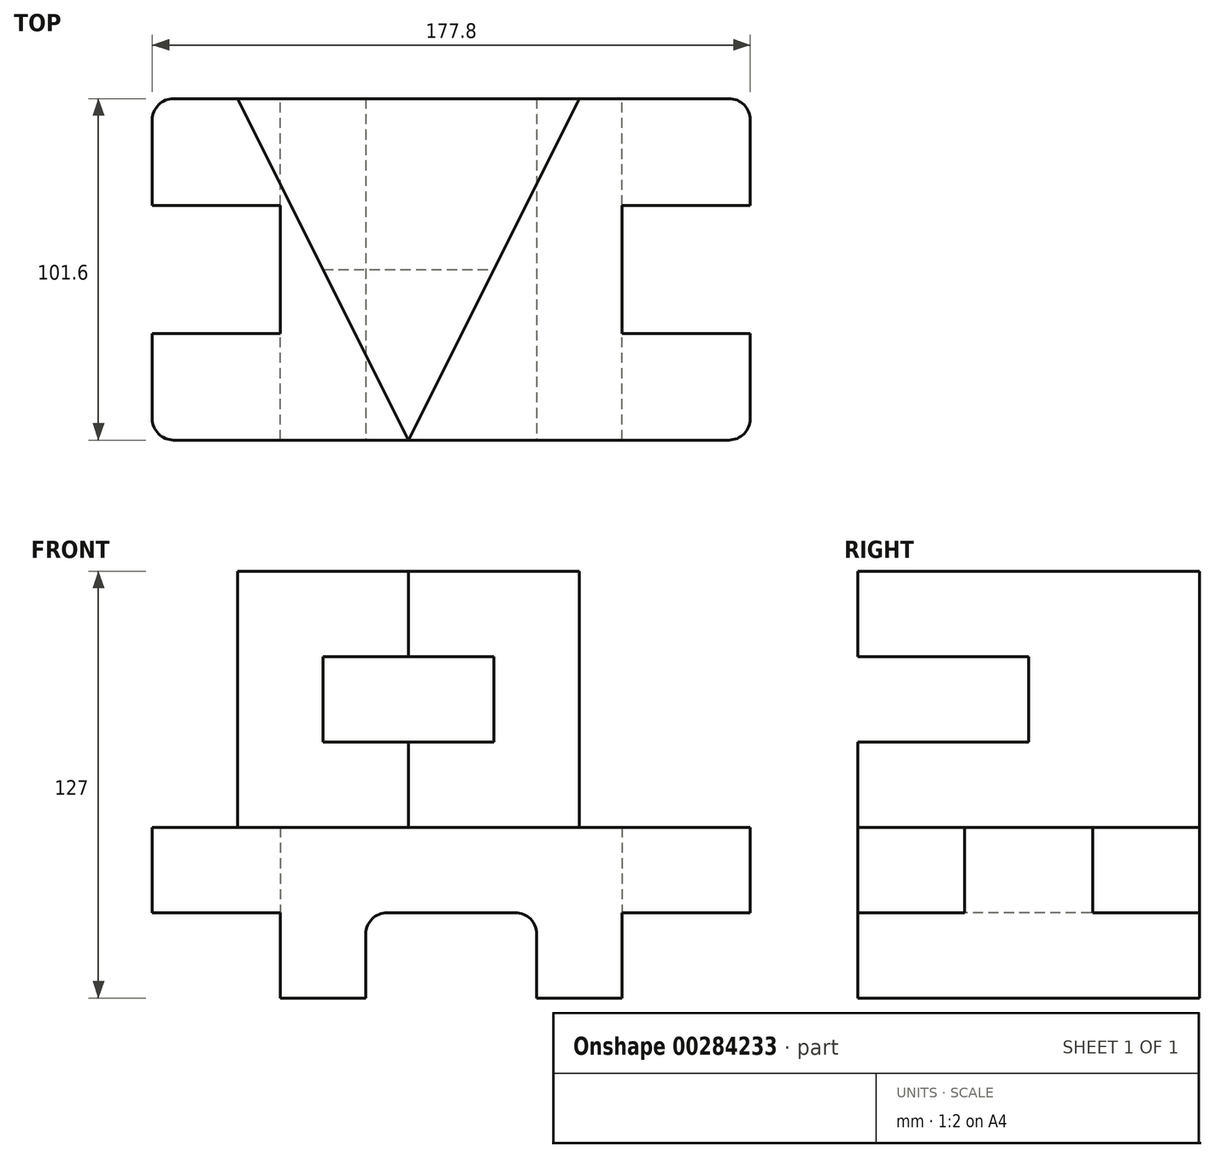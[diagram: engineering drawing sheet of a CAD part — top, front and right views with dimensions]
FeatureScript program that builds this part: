
annotation { "Feature Type Name" : "Feature", "Feature Type Description" : "" }
export const myFeature = defineFeature(function(context is Context, id is Id, definition is map)
    precondition{}
    {
        {
            var Q0;
            Q0=qCreatedBy(makeId("Front.planeOp"),FACE);
            var sketch = newSketch(context, id + "F0", { "sketchPlane" : qUnion([Q0])});
            skLineSegment(sketch, "E0", {"start": v(0, 0) * mm, "end": v(0, 25.4) * mm});
            skLineSegment(sketch, "E1", {"start": v(0, 25.4) * mm, "end": v(-38.1, 25.4) * mm});
            skLineSegment(sketch, "E2", {"start": v(-38.1, 25.4) * mm, "end": v(-38.1, 50.8) * mm});
            skLineSegment(sketch, "E3", {"start": v(-38.1, 50.8) * mm, "end": v(139.7, 50.8) * mm});
            skLineSegment(sketch, "E4", {"start": v(139.7, 50.8) * mm, "end": v(139.7, 25.4) * mm});
            skLineSegment(sketch, "E5", {"start": v(139.7, 25.4) * mm, "end": v(101.6, 25.4) * mm});
            skLineSegment(sketch, "E6", {"start": v(101.6, 25.4) * mm, "end": v(101.6, 0) * mm});
            skLineSegment(sketch, "E7", {"start": v(101.6, 0) * mm, "end": v(0, 0) * mm});
            skSolve(sketch);
        }
        {
            var Q0;
            Q0 = qSketchRegion(id + "F0", true);
            extrude(context, id + "F1", {"entities" : qUnion([Q0]), "depth" : 101.6 * mm});
        }
        {
            var Q0;
            Q0=makeQuery(id+"F1.opExtrude","SWEPT_FACE",FACE,{"disambiguationData":[OSD([sQuery(id+"F0.wireOp",EDGE,"E4")])]});
            var sketch = newSketch(context, id + "F2", { "sketchPlane" : qUnion([Q0])});
            skLineSegment(sketch, "E8.bottom", {"start": v(-69.85, 50.8) * mm, "end": v(-31.75, 50.8) * mm});
            skLineSegment(sketch, "E8.top", {"start": v(-69.85, 25.4) * mm, "end": v(-31.75, 25.4) * mm});
            skLineSegment(sketch, "E8.left", {"start": v(-69.85, 50.8) * mm, "end": v(-69.85, 25.4) * mm});
            skLineSegment(sketch, "E8.right", {"start": v(-31.75, 50.8) * mm, "end": v(-31.75, 25.4) * mm});
            skSolve(sketch);
        }
        {
            var Q0;
            Q0 = qSketchRegion(id + "F2", true);
            extrude(context, id + "F3", {"entities" : qUnion([Q0]), "operationType" : NewBodyOperationType.REMOVE, "oppositeDirection" : true, "depth" : 38.1 * mm});
        }
        {
            var Q0;
            Q0=makeQuery(id+"F1.opExtrude","SWEPT_FACE",FACE,{"disambiguationData":[OSD([sQuery(id+"F0.wireOp",EDGE,"E2")])]});
            var sketch = newSketch(context, id + "F4", { "sketchPlane" : qUnion([Q0])});
            skLineSegment(sketch, "E9.bottom", {"start": v(31.75, 50.8) * mm, "end": v(69.85, 50.8) * mm});
            skLineSegment(sketch, "E9.top", {"start": v(31.75, 25.4) * mm, "end": v(69.85, 25.4) * mm});
            skLineSegment(sketch, "E9.left", {"start": v(31.75, 50.8) * mm, "end": v(31.75, 25.4) * mm});
            skLineSegment(sketch, "E9.right", {"start": v(69.85, 50.8) * mm, "end": v(69.85, 25.4) * mm});
            skSolve(sketch);
        }
        {
            var Q0;
            Q0 = qSketchRegion(id + "F4", true);
            extrude(context, id + "F5", {"entities" : qUnion([Q0]), "operationType" : NewBodyOperationType.REMOVE, "oppositeDirection" : true, "depth" : 38.1 * mm});
        }
        {
            var Q0;
            Q0=makeQuery(id+"F1.opExtrude","CAP_EDGE",EDGE,{"disambiguationData":[OSD([sQuery(id+"F0.wireOp",EDGE,"E4")])],"isStart":false});
            var Q1;
            Q1=makeQuery(id+"F1.opExtrude","CAP_EDGE",EDGE,{"disambiguationData":[OSD([sQuery(id+"F0.wireOp",EDGE,"E4")])],"isStart":true});
            var Q2;
            Q2=makeQuery(id+"F1.opExtrude","CAP_EDGE",EDGE,{"disambiguationData":[OSD([sQuery(id+"F0.wireOp",EDGE,"E2")])],"isStart":false});
            var Q3;
            Q3=makeQuery(id+"F1.opExtrude","CAP_EDGE",EDGE,{"disambiguationData":[OSD([sQuery(id+"F0.wireOp",EDGE,"E2")])],"isStart":true});
            fillet(context, id + "F6", {"entities" : qUnion([Q0, Q1, Q2, Q3]), "radius" : 6.35 * mm, "tangentPropagation" : true, "allowEdgeOverflow" : false});
        }
        {
            var Q0;
            Q0=makeQuery(id+"F1.opExtrude","CAP_FACE",FACE,{"disambiguationData":[OSD([sQuery(id+"F0.wireOp",EDGE,"E0"),sQuery(id+"F0.wireOp",EDGE,"E1"),sQuery(id+"F0.wireOp",EDGE,"E2"),sQuery(id+"F0.wireOp",EDGE,"E3"),sQuery(id+"F0.wireOp",EDGE,"E4"),sQuery(id+"F0.wireOp",EDGE,"E5"),sQuery(id+"F0.wireOp",EDGE,"E6"),sQuery(id+"F0.wireOp",EDGE,"E7")])],"isStart":false});
            var sketch = newSketch(context, id + "F7", { "sketchPlane" : qUnion([Q0])});
            skLineSegment(sketch, "E10.bottom", {"start": v(25.4, 0) * mm, "end": v(76.2, 0) * mm});
            skLineSegment(sketch, "E10.top", {"start": v(25.4, 25.4) * mm, "end": v(76.2, 25.4) * mm});
            skLineSegment(sketch, "E10.left", {"start": v(25.4, 0) * mm, "end": v(25.4, 25.4) * mm});
            skLineSegment(sketch, "E10.right", {"start": v(76.2, 0) * mm, "end": v(76.2, 25.4) * mm});
            skSolve(sketch);
        }
        {
            var Q0;
            Q0 = qSketchRegion(id + "F7", true);
            extrude(context, id + "F8", {"entities" : qUnion([Q0]), "operationType" : NewBodyOperationType.REMOVE, "endBound" : BoundingType.THROUGH_ALL, "oppositeDirection" : true, "depth" : 25.4 * mm});
        }
        {
            var Q0;
            Q0=makeQuery(id+"F8.boolean.opBoolean","COPY",EDGE,{"derivedFrom":makeQuery(id+"F8.opExtrude","SWEPT_EDGE",EDGE,{"disambiguationData":[OSD([sQuery(id+"F7.wireOp",EDGE,"E10.top"),sQuery(id+"F7.wireOp",EDGE,"E10.left")])]})});
            var Q1;
            Q1=makeQuery(id+"F8.boolean.opBoolean","COPY",EDGE,{"derivedFrom":makeQuery(id+"F8.opExtrude","SWEPT_EDGE",EDGE,{"disambiguationData":[OSD([sQuery(id+"F7.wireOp",EDGE,"E10.top"),sQuery(id+"F7.wireOp",EDGE,"E10.right")])]})});
            fillet(context, id + "F9", {"entities" : qUnion([Q0, Q1]), "radius" : 6.35 * mm, "tangentPropagation" : true, "allowEdgeOverflow" : false});
        }
        {
            var Q0;
            Q0=makeQuery(id+"F1.opExtrude","SWEPT_FACE",FACE,{"disambiguationData":[OSD([sQuery(id+"F0.wireOp",EDGE,"E3")])]});
            var sketch = newSketch(context, id + "F10", { "sketchPlane" : qUnion([Q0])});
            skLineSegment(sketch, "E11.bottom", {"start": v(-12.7, 0) * mm, "end": v(88.9, 0) * mm});
            skLineSegment(sketch, "E11.top", {"start": v(-12.7, -101.6) * mm, "end": v(88.9, -101.6) * mm});
            skLineSegment(sketch, "E11.left", {"start": v(-12.7, 0) * mm, "end": v(-12.7, -101.6) * mm});
            skLineSegment(sketch, "E11.right", {"start": v(88.9, 0) * mm, "end": v(88.9, -101.6) * mm});
            skSolve(sketch);
        }
        {
            var Q0;
            Q0 = qSketchRegion(id + "F10", true);
            extrude(context, id + "F11", {"entities" : qUnion([Q0]), "operationType" : NewBodyOperationType.ADD, "depth" : 76.2 * mm});
        }
        {
            var Q0;
            Q0=makeQuery(id+"F11.opExtrude","CAP_FACE",FACE,{"disambiguationData":[OSD([sQuery(id+"F10.wireOp",EDGE,"E11.bottom"),sQuery(id+"F10.wireOp",EDGE,"E11.top"),sQuery(id+"F10.wireOp",EDGE,"E11.left"),sQuery(id+"F10.wireOp",EDGE,"E11.right")])],"isStart":false});
            var sketch = newSketch(context, id + "F12", { "sketchPlane" : qUnion([Q0])});
            skLineSegment(sketch, "E12", {"start": v(-12.7, 0) * mm, "end": v(38.1, -101.6) * mm});
            skLineSegment(sketch, "E13", {"start": v(38.1, -101.6) * mm, "end": v(-12.7, -101.6) * mm});
            skLineSegment(sketch, "E14", {"start": v(-12.7, 0) * mm, "end": v(-12.7, -101.6) * mm});
            skLineSegment(sketch, "E15", {"start": v(38.1, -101.6) * mm, "end": v(88.9, 0) * mm});
            skLineSegment(sketch, "E16", {"start": v(88.9, 0) * mm, "end": v(88.9, -101.6) * mm});
            skLineSegment(sketch, "E17", {"start": v(38.1, -101.6) * mm, "end": v(88.9, -101.6) * mm});
            skSolve(sketch);
        }
        {
            var Q0;
            Q0 = qSketchRegion(id + "F12", true);
            extrude(context, id + "F13", {"entities" : qUnion([Q0]), "operationType" : NewBodyOperationType.REMOVE, "oppositeDirection" : true, "depth" : 76.2 * mm});
        }
        {
            var Q0;
            Q0=makeQuery(id+"F11.opExtrude","CAP_FACE",FACE,{"disambiguationData":[OSD([sQuery(id+"F10.wireOp",EDGE,"E11.bottom"),sQuery(id+"F10.wireOp",EDGE,"E11.top"),sQuery(id+"F10.wireOp",EDGE,"E11.left"),sQuery(id+"F10.wireOp",EDGE,"E11.right")])],"isStart":false});
            var sketch = newSketch(context, id + "F14", { "sketchPlane" : qUnion([Q0])});
            skLineSegment(sketch, "E18", {"start": v(12.7, -50.8) * mm, "end": v(63.5, -50.8) * mm});
            skLineSegment(sketch, "E19", {"start": v(63.5, -50.8) * mm, "end": v(38.1, -101.6) * mm});
            skLineSegment(sketch, "E20", {"start": v(38.1, -101.6) * mm, "end": v(12.7, -50.8) * mm});
            skSolve(sketch);
        }
        {
            var Q0;
            Q0 = qSketchRegion(id + "F14", true);
            extrude(context, id + "F15", {"entities" : qUnion([Q0]), "operationType" : NewBodyOperationType.REMOVE, "oppositeDirection" : true, "depth" : 50.8 * mm, "hasSecondDirection" : true, "secondDirectionOppositeDirection" : true, "secondDirectionDepth" : 25.4 * mm});
        }
    });
